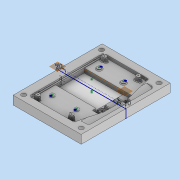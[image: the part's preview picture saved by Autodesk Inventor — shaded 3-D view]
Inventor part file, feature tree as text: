
AUTODESK INVENTOR PART (.ipt)
format: ipt  version: 2022 (Build 260153070, 153G)  size: 2,422,272 bytes
history: native  units: mm
features: other x45, surface_op x16, extrude x14, sketch x10, plane x7, thicken_offset x7, projected_geometry x3, boolean_combine x2, mirror x2, split x1, revolve x1, pattern_linear x1
ambient origin geometry x8: Origin, YZ Plane, XZ Plane, XY Plane, X Axis, Y Axis, Z Axis, Center Point
bodies: Solid2 (feature_tree), Solid5 (feature_tree), Solid6 (feature_tree), Solid1 (feature_tree)
feature tree (109):
  other  "P00173-09-003.ipt"
  other  "P00173-09-010.ipt"
  other  "Blocks"
  sketch  "Sketch5"  dims[d0=10.0mm]
  plane  "Work Plane1"
  sketch  "Sketch6"  dims[d188=24.0mm d189=25.0mm d194=9.5mm d201=21.0mm d202=2.0mm d203=12.5mm d204=2.1mm d1=20.0mm]
  plane  "Work Plane2"
  sketch  "Sketch11"  dims[d13=15.0mm d14=7.0mm d15=0.0mm]
  extrude  "Extrusion1"  Depth=20.0mm
  split  "Split1"
  extrude  "Extrusion6"  Depth=20.0mm
  surface_op  "Extend1"
  surface_op  "Extend2"
  plane  "Work Plane4"
  sketch  "Sketch15"  dims[d16=20.0mm d17=8.0mm]
  surface_op  "Extend3"
  surface_op  "Extend4"
  plane  "Work Plane5"
  surface_op  "Trim1"
  surface_op  "Trim2"
  surface_op  "Trim3"
  surface_op  "Trim4"
  sketch  "Sketch16"  dims[d18=7.0mm d19=0.0mm]
  surface_op  "Stitch Surface6"
  surface_op  "Stitch Surface3"
  surface_op  "Stitch Surface7"
  boolean_combine  "Combine1"
  extrude  "Extrusion4"  Depth=10.0mm TaperAngle=0.0deg
  extrude  "Extrusion5"  Depth=7.0mm TaperAngle=0.0deg
  thicken_offset  "Thicken1"
  thicken_offset  "Thicken2"
  thicken_offset  "Thicken3"
  thicken_offset  "Thicken4"
  thicken_offset  "Thicken5"
  thicken_offset  "Thicken6"
  thicken_offset  "Thicken7"
  revolve  "Revolution1"  [1 undecoded]
  pattern_linear  "Rectangular Pattern1"  Spacing1=0.2mm  [1 undecoded]
  mirror  "Mirror1"
  boolean_combine  "Combine2"
  sketch  "Sketch17"  dims[d20=0.2mm]
  extrude  "Extrusion7"  Depth=4.0mm
  extrude  "Extrusion8"  Depth=4.0mm
  extrude  "Extrusion9"  Depth=4.0mm
  extrude  "Extrusion10"  Depth=4.0mm
  extrude  "Extrusion11"  Depth=4.0mm
  extrude  "Extrusion12"  Depth=4.0mm
  plane  "Work Plane8"
  sketch  "Sketch19"  dims[d21=0.2mm]
  extrude  "Extrusion13"  Depth=4.0mm
  mirror  "Mirror2"
  sketch  "Sketch20"  dims[d22=0.2mm d23=0.2mm d24=0.2mm d25=0.2mm d26=0.2mm d27=0.2mm d28=0.2mm d29=0.2mm d30=0.2mm d31=0.2mm d32=0.2mm d33=0.2mm d44=15.0mm d45=15.0mm d46=6.0mm d47=90.0deg d48=20.0mm d50=155.0mm d51=4.0mm d56=1.0mm d57=0.0mm d58=5.75mm d59=5.5mm d60=1.0mm d61=1.0mm d62=1.0mm d63=1.0mm d64=6.0mm d65=5.75mm d71=20.0mm d74=5.0mm d75=0.0mm d76=5.0mm d77=0.0mm d78=3.0mm d79=1.0mm d83=1.0mm d84=0.0mm d85=5.0mm d86=0.0mm d87=3.0mm d88=1.0mm d89=4.5mm d92=5.0mm d93=0.349066mm d95=3.0mm d96=1.0mm d97=4.195888mm d98=4.0mm d99=0.0mm d100=6.0mm d101=2.0mm d102=3.0mm d103=6.0mm d104=2.0mm d105=10.0mm d106=0.349066mm d107=4.0mm d108=0.0mm d109=7.0mm d110=3.0mm d111=3.0mm d112=8.0mm d113=0.0mm d114=2.5mm d115=2.0mm d116=2.5mm d117=2.0mm d118=2.5mm d119=7.5mm d120=2.5mm d121=2.5mm d122=2.5mm d123=7.5mm d124=0.0mm d125=6.5mm d126=0.0mm d127=6.75mm d128=0.0mm]
  extrude  "Extrusion14"  Depth=4.0mm
  extrude  "Extrusion15"  Depth=4.0mm
  extrude  "Extrusion16"  Depth=4.0mm
  other  "TaggingFeature1"
  other  "Camera_Top"
  other  "Side"
  other  "Bottom"
  other  "Top_Housing"
  other  "Screen_Hole"
  other  "Solid13::P00173-09-010.ipt"
  other  "Srf3"
  other  "Srf4"
  other  "Srf5"
  other  "Srf6"
  other  "Srf7"
  sketch  "Sketch9"  dims[d2=20.0mm d4=20.0mm]
  sketch  "Sketch10"  dims[d5=10.0mm d6=10.0mm d7=0.0mm]
  other  "Screen_Hole_1"
  other  "Srf9"
  other  "Srf10"
  other  "Screen_Mount_1"
  other  "Screen_Mount_Side"
  other  "Srf11"
  other  "Srf12"
  plane  "Work Plane - Cup_Draft"
  plane  "Work Plane - Cup_Draft_2"
  other  "Srf17"
  other  "Srf19"
  surface_op  "Stitch Surface5"
  other  "Srf20"
  other  "Srf21"
  other  "Srf22"
  other  "Srf23"
  other  "Block2"
  other  "Block2_1"
  projected_geometry  "Projected Loop1"
  other  "OffsetSrf2"
  other  "OffsetSrf3"
  other  "Camera_Top:1"
  other  "Srf21::Derived"
  other  "Srf26::Derived"
  other  "Srf32::Derived"
  other  "Srf33::Derived"
  other  "Srf34::Derived"
  projected_geometry  "Project Cut Edges3"
  other  "Srf12::Derived"
  other  "Srf15::Derived"
  projected_geometry  "Project Cut Edges5"
  surface_op  "Boundary Patch6"
  surface_op  "Boundary Patch8"
  other  "Block2:1"
  other  "Block2:2"
  other  "Block2:3"
  other  "Block2:4"
  other  "Block2:6"
  surface_op  "Boundary Patch7"
  surface_op  "Boundary Patch5"
note: 2 required parameter values undecoded (feature->parameter linkage not recoverable at this tier; creation-order binding heuristic only, values carry confidence <= 0.55)